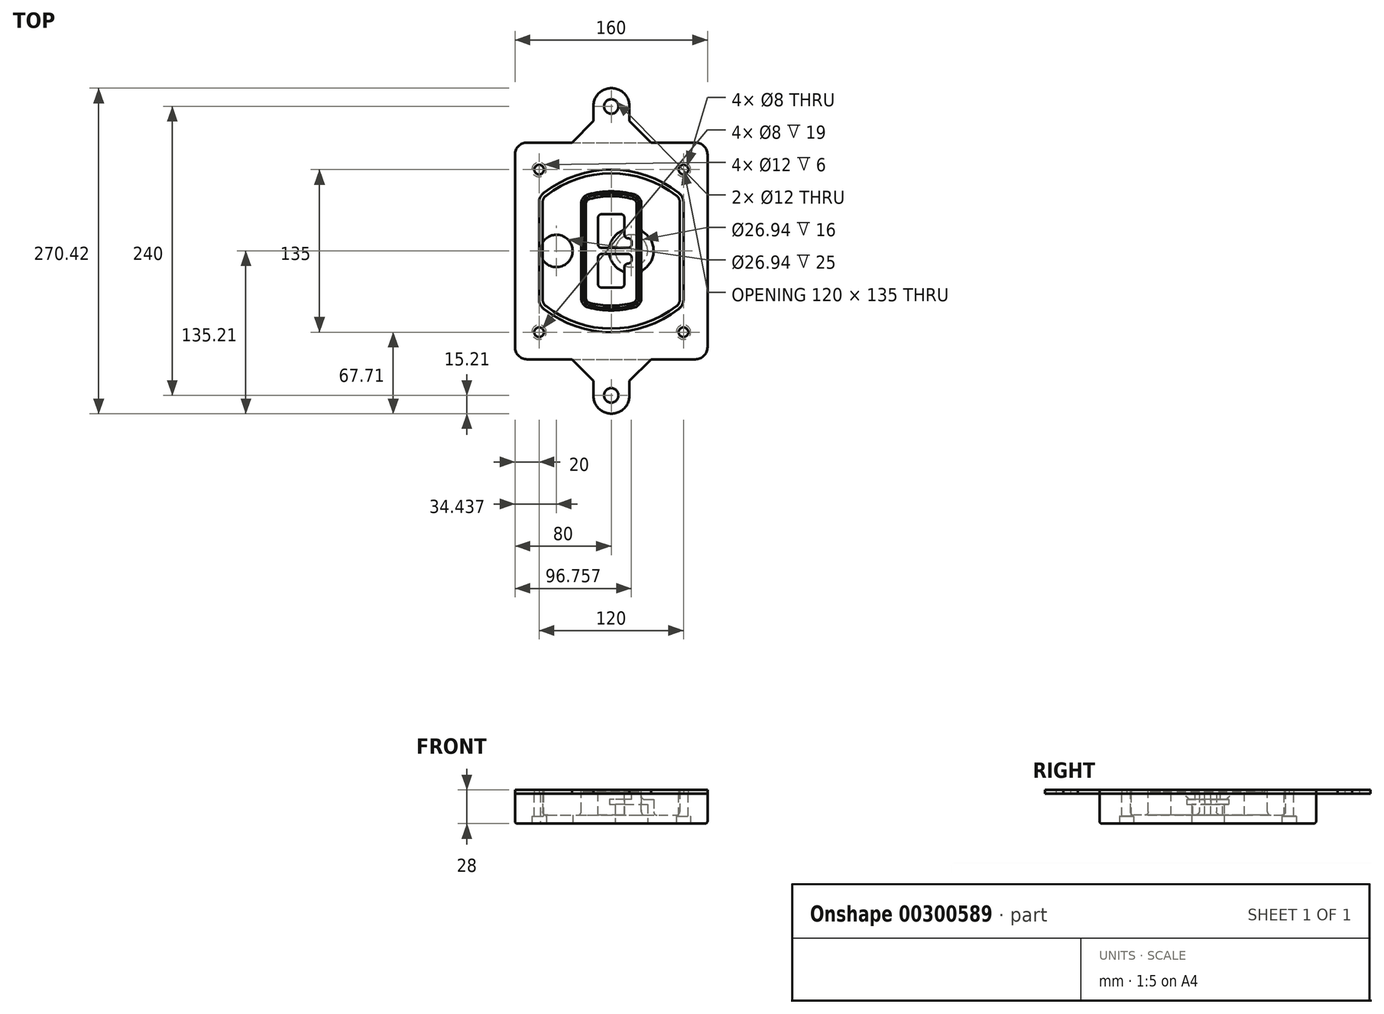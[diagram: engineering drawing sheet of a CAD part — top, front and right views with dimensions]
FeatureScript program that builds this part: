
annotation { "Feature Type Name" : "Feature", "Feature Type Description" : "" }
export const myFeature = defineFeature(function(context is Context, id is Id, definition is map)
    precondition{}
    {
        {
            var Q0;
            Q0=qCreatedBy(makeId("Top.planeOp"),FACE);
            var sketch = newSketch(context, id + "F0", { "sketchPlane" : qUnion([Q0])});
            skPoint(sketch, "E0.rect.middle", {"position": v(0, 0) * mm});
            skLineSegment(sketch, "E1.bottom", {"start": v(-70, -90) * mm, "end": v(70, -90) * mm});
            skLineSegment(sketch, "E1.top", {"start": v(-70, 90) * mm, "end": v(70, 90) * mm});
            skLineSegment(sketch, "E1.left", {"start": v(-80, -80) * mm, "end": v(-80, 80) * mm});
            skLineSegment(sketch, "E1.right", {"start": v(80, -80) * mm, "end": v(80, 80) * mm});
            skLineSegment(sketch, "E2", {"start": v(-80, 90) * mm, "end": v(80, -90) * mm, "construction": true});
            skLineSegment(sketch, "E3", {"start": v(80, 90) * mm, "end": v(-80, -90) * mm, "construction": true});
            skCircle(sketch, "E4", {"center": v(-60, 67.5) * mm, "radius": 4 * mm});
            skCircle(sketch, "E5", {"center": v(60, 67.5) * mm, "radius": 4 * mm});
            skCircle(sketch, "E6", {"center": v(60, -67.5) * mm, "radius": 4 * mm});
            skCircle(sketch, "E7", {"center": v(-60, -67.5) * mm, "radius": 4 * mm});
            skLineSegment(sketch, "E8", {"start": v(-60, 67.5) * mm, "end": v(60, 67.5) * mm, "construction": true});
            skLineSegment(sketch, "E9", {"start": v(60, 67.5) * mm, "end": v(60, -67.5) * mm, "construction": true});
            skLineSegment(sketch, "E10", {"start": v(60, -67.5) * mm, "end": v(-60, -67.5) * mm, "construction": true});
            skLineSegment(sketch, "E11", {"start": v(-60, -67.5) * mm, "end": v(-60, 67.5) * mm, "construction": true});
            skLineSegment(sketch, "E12", {"start": v(-60, 40.3) * mm, "end": v(-60, -40.3) * mm});
            skLineSegment(sketch, "E13", {"start": v(60, 40.3) * mm, "end": v(60, -40.3) * mm});
            skArc(sketch, "E14", {"start": v(56.15, 48.18) * mm, "mid": v(0, 67.5) * mm, "end": v(-56.15, 48.18) * mm});
            skArc(sketch, "E15", {"start": v(-56.15, -48.18) * mm, "mid": v(0, -67.5) * mm, "end": v(56.15, -48.18) * mm});
            skLineSegment(sketch, "E16", {"start": v(-60, 0) * mm, "end": v(60, 0) * mm, "construction": true});
            skPoint(sketch, "E17.visualSharp", {"position": v(-60, -45) * mm});
            skArc(sketch, "E17.filletArc", {"start": v(-60, -40.3) * mm, "mid": v(-58.99, -44.68) * mm, "end": v(-56.15, -48.18) * mm});
            skPoint(sketch, "E18.visualSharp", {"position": v(-60, 45) * mm});
            skArc(sketch, "E18.filletArc", {"start": v(-56.15, 48.18) * mm, "mid": v(-58.99, 44.68) * mm, "end": v(-60, 40.3) * mm});
            skPoint(sketch, "E19.visualSharp", {"position": v(60, 45) * mm});
            skArc(sketch, "E19.filletArc", {"start": v(60, 40.3) * mm, "mid": v(58.99, 44.68) * mm, "end": v(56.15, 48.18) * mm});
            skPoint(sketch, "E20.visualSharp", {"position": v(60, -45) * mm});
            skArc(sketch, "E20.filletArc", {"start": v(56.15, -48.18) * mm, "mid": v(58.99, -44.68) * mm, "end": v(60, -40.3) * mm});
            skPoint(sketch, "E21.visualSharp", {"position": v(-80, 90) * mm});
            skArc(sketch, "E21.filletArc", {"start": v(-70, 90) * mm, "mid": v(-77.07, 87.07) * mm, "end": v(-80, 80) * mm});
            skPoint(sketch, "E22.visualSharp", {"position": v(80, 90) * mm});
            skArc(sketch, "E22.filletArc", {"start": v(80, 80) * mm, "mid": v(77.07, 87.07) * mm, "end": v(70, 90) * mm});
            skPoint(sketch, "E23.visualSharp", {"position": v(80, -90) * mm});
            skArc(sketch, "E23.filletArc", {"start": v(70, -90) * mm, "mid": v(77.07, -87.07) * mm, "end": v(80, -80) * mm});
            skPoint(sketch, "E24.visualSharp", {"position": v(-80, -90) * mm});
            skArc(sketch, "E24.filletArc", {"start": v(-80, -80) * mm, "mid": v(-77.07, -87.07) * mm, "end": v(-70, -90) * mm});
            skArc(sketch, "E25.0", {"start": v(57, 40.3) * mm, "mid": v(56.3, 43.36) * mm, "end": v(54.3, 45.81) * mm});
            skLineSegment(sketch, "E25.1", {"start": v(57, 40.3) * mm, "end": v(57, -40.3) * mm});
            skArc(sketch, "E25.2", {"start": v(54.3, -45.81) * mm, "mid": v(56.3, -43.36) * mm, "end": v(57, -40.3) * mm});
            skArc(sketch, "E25.3", {"start": v(-54.3, -45.81) * mm, "mid": v(0, -64.5) * mm, "end": v(54.3, -45.81) * mm});
            skArc(sketch, "E25.4", {"start": v(-57, -40.3) * mm, "mid": v(-56.3, -43.36) * mm, "end": v(-54.3, -45.81) * mm});
            skArc(sketch, "E25.5", {"start": v(54.3, 45.81) * mm, "mid": v(0, 64.5) * mm, "end": v(-54.3, 45.81) * mm});
            skLineSegment(sketch, "E25.6", {"start": v(-57, 40.3) * mm, "end": v(-57, -40.3) * mm});
            skArc(sketch, "E25.7", {"start": v(-54.3, 45.81) * mm, "mid": v(-56.3, 43.36) * mm, "end": v(-57, 40.3) * mm});
            skArc(sketch, "E26.0", {"start": v(-58.62, 51.33) * mm, "mid": v(-62.58, 46.43) * mm, "end": v(-64, 40.3) * mm});
            skArc(sketch, "E26.1", {"start": v(58.62, 51.33) * mm, "mid": v(0, 71.5) * mm, "end": v(-58.62, 51.33) * mm});
            skArc(sketch, "E26.2", {"start": v(64, 40.3) * mm, "mid": v(62.58, 46.43) * mm, "end": v(58.62, 51.33) * mm});
            skLineSegment(sketch, "E26.3", {"start": v(64, 40.3) * mm, "end": v(64, -40.3) * mm});
            skArc(sketch, "E26.4", {"start": v(58.62, -51.33) * mm, "mid": v(62.58, -46.43) * mm, "end": v(64, -40.3) * mm});
            skLineSegment(sketch, "E26.5", {"start": v(-64, 40.3) * mm, "end": v(-64, -40.3) * mm});
            skArc(sketch, "E26.6", {"start": v(-58.62, -51.33) * mm, "mid": v(0, -71.5) * mm, "end": v(58.62, -51.33) * mm});
            skArc(sketch, "E26.7", {"start": v(-64, -40.3) * mm, "mid": v(-62.58, -46.43) * mm, "end": v(-58.62, -51.33) * mm});
            skSolve(sketch);
        }
        {
            var Q0;
            Q0=makeQuery(id+"F0.imprint","IMPRINT",FACE,{"disambiguationData":[TD([[makeQuery(id+"F0.imprint","IMPRINT",EDGE,{"derivedFrom":sQuery(id+"F0.wireOp",EDGE,"E1.bottom")}),1.0]])]});
            var Q1;
            Q1=makeQuery(id+"F0.imprint","IMPRINT",FACE,{"disambiguationData":[TD([[makeQuery(id+"F0.imprint","IMPRINT",EDGE,{"derivedFrom":sQuery(id+"F0.wireOp",EDGE,"E12")}),1.0]])]});
            var Q2;
            Q2=makeQuery(id+"F0.imprint","IMPRINT",FACE,{"disambiguationData":[TD([[makeQuery(id+"F0.imprint","IMPRINT",EDGE,{"derivedFrom":sQuery(id+"F0.wireOp",EDGE,"E25.0")}),1.0]])]});
            var Q3;
            Q3=makeQuery(id+"F0.imprint","IMPRINT",FACE,{"disambiguationData":[TD([[makeQuery(id+"F0.imprint","IMPRINT",EDGE,{"derivedFrom":sQuery(id+"F0.wireOp",EDGE,"E12")}),-1.0]])]});
            extrude(context, id + "F1", {"entities" : qUnion([Q0, Q1, Q2, Q3]), "oppositeDirection" : true, "depth" : 25 * mm});
        }
        {
            var Q0;
            Q0=makeQuery(id+"F0.imprint","IMPRINT",FACE,{"disambiguationData":[TD([[makeQuery(id+"F0.imprint","IMPRINT",EDGE,{"derivedFrom":sQuery(id+"F0.wireOp",EDGE,"E12")}),1.0]])]});
            extrude(context, id + "F2", {"entities" : qUnion([Q0]), "operationType" : NewBodyOperationType.ADD, "depth" : 3 * mm});
        }
        {
            var Q0;
            Q0=makeQuery(id+"F0.imprint","IMPRINT",FACE,{"disambiguationData":[TD([[makeQuery(id+"F0.imprint","IMPRINT",EDGE,{"derivedFrom":sQuery(id+"F0.wireOp",EDGE,"E25.0")}),1.0]])]});
            extrude(context, id + "F3", {"entities" : qUnion([Q0]), "operationType" : NewBodyOperationType.REMOVE, "oppositeDirection" : true, "depth" : 18 * mm});
        }
        {
            var Q0;
            Q0=makeQuery(id+"F2.opExtrude","CAP_FACE",FACE,{"disambiguationData":[OSD([sQuery(id+"F0.wireOp",EDGE,"E12"),sQuery(id+"F0.wireOp",EDGE,"E13"),sQuery(id+"F0.wireOp",EDGE,"E14"),sQuery(id+"F0.wireOp",EDGE,"E15"),sQuery(id+"F0.wireOp",EDGE,"E17.filletArc"),sQuery(id+"F0.wireOp",EDGE,"E18.filletArc"),sQuery(id+"F0.wireOp",EDGE,"E19.filletArc"),sQuery(id+"F0.wireOp",EDGE,"E20.filletArc"),sQuery(id+"F0.wireOp",EDGE,"E25.0"),sQuery(id+"F0.wireOp",EDGE,"E25.1"),sQuery(id+"F0.wireOp",EDGE,"E25.2"),sQuery(id+"F0.wireOp",EDGE,"E25.3"),sQuery(id+"F0.wireOp",EDGE,"E25.4"),sQuery(id+"F0.wireOp",EDGE,"E25.5"),sQuery(id+"F0.wireOp",EDGE,"E25.6"),sQuery(id+"F0.wireOp",EDGE,"E25.7")])],"isStart":false});
            var sketch = newSketch(context, id + "F4", { "sketchPlane" : qUnion([Q0])});
            skArc(sketch, "E27.0", {"start": v(-19.08, -46.97) * mm, "mid": v(0, -49.5) * mm, "end": v(19.08, -46.97) * mm});
            skArc(sketch, "E28.0", {"start": v(19.08, 46.97) * mm, "mid": v(0, 49.5) * mm, "end": v(-19.08, 46.97) * mm});
            skLineSegment(sketch, "E29", {"start": v(-25, 39.25) * mm, "end": v(-25, -39.25) * mm});
            skLineSegment(sketch, "E30", {"start": v(25, 39.25) * mm, "end": v(25, -39.25) * mm});
            skLineSegment(sketch, "E31", {"start": v(-25, 45.1) * mm, "end": v(25, 45.1) * mm, "construction": true});
            skLineSegment(sketch, "E32", {"start": v(-25, -45.1) * mm, "end": v(25, -45.1) * mm, "construction": true});
            skPoint(sketch, "E33.visualSharp", {"position": v(-25, 45.1) * mm});
            skArc(sketch, "E33.filletArc", {"start": v(-19.08, 46.97) * mm, "mid": v(-23.35, 44.11) * mm, "end": v(-25, 39.25) * mm});
            skPoint(sketch, "E34.visualSharp", {"position": v(25, 45.1) * mm});
            skArc(sketch, "E34.filletArc", {"start": v(25, 39.25) * mm, "mid": v(23.35, 44.11) * mm, "end": v(19.08, 46.97) * mm});
            skPoint(sketch, "E35.visualSharp", {"position": v(25, -45.1) * mm});
            skArc(sketch, "E35.filletArc", {"start": v(19.08, -46.97) * mm, "mid": v(23.35, -44.11) * mm, "end": v(25, -39.25) * mm});
            skPoint(sketch, "E36.visualSharp", {"position": v(-25, -45.1) * mm});
            skArc(sketch, "E36.filletArc", {"start": v(-25, -39.25) * mm, "mid": v(-23.35, -44.11) * mm, "end": v(-19.08, -46.97) * mm});
            skArc(sketch, "E37.0", {"start": v(54.3, 45.81) * mm, "mid": v(0, 64.5) * mm, "end": v(-54.3, 45.81) * mm});
            skArc(sketch, "E37.1", {"start": v(-54.3, 45.81) * mm, "mid": v(-56.3, 43.36) * mm, "end": v(-57, 40.3) * mm});
            skLineSegment(sketch, "E37.2", {"start": v(-57, 40.3) * mm, "end": v(-57, -40.3) * mm});
            skArc(sketch, "E37.3", {"start": v(-57, -40.3) * mm, "mid": v(-56.3, -43.36) * mm, "end": v(-54.3, -45.81) * mm});
            skArc(sketch, "E37.4", {"start": v(-54.3, -45.81) * mm, "mid": v(0, -64.5) * mm, "end": v(54.3, -45.81) * mm});
            skArc(sketch, "E37.5", {"start": v(54.3, -45.81) * mm, "mid": v(56.3, -43.36) * mm, "end": v(57, -40.3) * mm});
            skLineSegment(sketch, "E37.6", {"start": v(57, 40.3) * mm, "end": v(57, -40.3) * mm});
            skArc(sketch, "E37.7", {"start": v(57, 40.3) * mm, "mid": v(56.3, 43.36) * mm, "end": v(54.3, 45.81) * mm});
            skLineSegment(sketch, "E38.0", {"start": v(23, 39.25) * mm, "end": v(23, -39.25) * mm});
            skArc(sketch, "E38.1", {"start": v(18.56, -45.04) * mm, "mid": v(21.76, -42.9) * mm, "end": v(23, -39.25) * mm});
            skArc(sketch, "E38.2", {"start": v(-18.56, -45.04) * mm, "mid": v(0, -47.5) * mm, "end": v(18.56, -45.04) * mm});
            skArc(sketch, "E38.3", {"start": v(-23, -39.25) * mm, "mid": v(-21.76, -42.9) * mm, "end": v(-18.56, -45.04) * mm});
            skLineSegment(sketch, "E38.4", {"start": v(-23, 39.25) * mm, "end": v(-23, -39.25) * mm});
            skArc(sketch, "E38.5", {"start": v(23, 39.25) * mm, "mid": v(21.76, 42.9) * mm, "end": v(18.56, 45.04) * mm});
            skArc(sketch, "E38.6", {"start": v(-18.56, 45.04) * mm, "mid": v(-21.76, 42.9) * mm, "end": v(-23, 39.25) * mm});
            skArc(sketch, "E38.7", {"start": v(18.56, 45.04) * mm, "mid": v(0, 47.5) * mm, "end": v(-18.56, 45.04) * mm});
            skArc(sketch, "E39.0", {"start": v(21, 39.25) * mm, "mid": v(20.18, 41.68) * mm, "end": v(18.04, 43.1) * mm});
            skLineSegment(sketch, "E39.1", {"start": v(21, 39.25) * mm, "end": v(21, -39.25) * mm});
            skArc(sketch, "E39.2", {"start": v(18.04, -43.1) * mm, "mid": v(20.18, -41.68) * mm, "end": v(21, -39.25) * mm});
            skArc(sketch, "E39.3", {"start": v(-18.04, -43.1) * mm, "mid": v(0, -45.5) * mm, "end": v(18.04, -43.1) * mm});
            skArc(sketch, "E39.4", {"start": v(-21, -39.25) * mm, "mid": v(-20.18, -41.68) * mm, "end": v(-18.04, -43.1) * mm});
            skArc(sketch, "E39.5", {"start": v(18.04, 43.1) * mm, "mid": v(0, 45.5) * mm, "end": v(-18.04, 43.1) * mm});
            skLineSegment(sketch, "E39.6", {"start": v(-21, 39.25) * mm, "end": v(-21, -39.25) * mm});
            skArc(sketch, "E39.7", {"start": v(-18.04, 43.1) * mm, "mid": v(-20.18, 41.68) * mm, "end": v(-21, 39.25) * mm});
            skLineSegment(sketch, "E40", {"start": v(-25, 0) * mm, "end": v(25, 0) * mm, "construction": true});
            skLineSegment(sketch, "E41", {"start": v(-11, 5.5) * mm, "end": v(-11, 27.5) * mm});
            skLineSegment(sketch, "E42", {"start": v(-8, 30.5) * mm, "end": v(8, 30.5) * mm});
            skLineSegment(sketch, "E43", {"start": v(11, 27.5) * mm, "end": v(11, 13.5) * mm});
            skLineSegment(sketch, "E44", {"start": v(14, 10.5) * mm, "end": v(14, 10.5) * mm});
            skLineSegment(sketch, "E45", {"start": v(17, 7.5) * mm, "end": v(17, 5.5) * mm});
            skLineSegment(sketch, "E46", {"start": v(14, 2.5) * mm, "end": v(-8, 2.5) * mm});
            skPoint(sketch, "E47.visualSharp", {"position": v(-11, 30.5) * mm});
            skArc(sketch, "E47.filletArc", {"start": v(-8, 30.5) * mm, "mid": v(-10.12, 29.62) * mm, "end": v(-11, 27.5) * mm});
            skPoint(sketch, "E48.visualSharp", {"position": v(11, 30.5) * mm});
            skArc(sketch, "E48.filletArc", {"start": v(11, 27.5) * mm, "mid": v(10.12, 29.62) * mm, "end": v(8, 30.5) * mm});
            skPoint(sketch, "E49.visualSharp", {"position": v(11, 10.5) * mm});
            skArc(sketch, "E49.filletArc", {"start": v(11, 13.5) * mm, "mid": v(11.88, 11.38) * mm, "end": v(14, 10.5) * mm});
            skPoint(sketch, "E50.visualSharp", {"position": v(17, 10.5) * mm});
            skArc(sketch, "E50.filletArc", {"start": v(17, 7.5) * mm, "mid": v(16.12, 9.62) * mm, "end": v(14, 10.5) * mm});
            skPoint(sketch, "E51.visualSharp", {"position": v(17, 2.5) * mm});
            skArc(sketch, "E51.filletArc", {"start": v(14, 2.5) * mm, "mid": v(16.12, 3.38) * mm, "end": v(17, 5.5) * mm});
            skPoint(sketch, "E52.visualSharp", {"position": v(-11, 2.5) * mm});
            skArc(sketch, "E52.filletArc", {"start": v(-11, 5.5) * mm, "mid": v(-10.12, 3.38) * mm, "end": v(-8, 2.5) * mm});
            skLineSegment(sketch, "E53.0.MirrorCS", {"start": v(14, -2.5) * mm, "end": v(-8, -2.5) * mm});
            skArc(sketch, "E54.0.MirrorCS", {"start": v(-11, -5.5) * mm, "mid": v(-10.12, -3.38) * mm, "end": v(-8, -2.5) * mm});
            skLineSegment(sketch, "E55.0.MirrorCS", {"start": v(-11, -5.5) * mm, "end": v(-11, -27.5) * mm});
            skArc(sketch, "E56.0.MirrorCS", {"start": v(-8, -30.5) * mm, "mid": v(-10.12, -29.62) * mm, "end": v(-11, -27.5) * mm});
            skLineSegment(sketch, "E57.0.MirrorCS", {"start": v(-8, -30.5) * mm, "end": v(8, -30.5) * mm});
            skArc(sketch, "E58.0.MirrorCS", {"start": v(11, -27.5) * mm, "mid": v(10.12, -29.62) * mm, "end": v(8, -30.5) * mm});
            skLineSegment(sketch, "E59.0.MirrorCS", {"start": v(11, -27.5) * mm, "end": v(11, -13.5) * mm});
            skArc(sketch, "E60.0.MirrorCS", {"start": v(11, -13.5) * mm, "mid": v(11.88, -11.38) * mm, "end": v(14, -10.5) * mm});
            skArc(sketch, "E61.0.MirrorCS", {"start": v(17, -7.5) * mm, "mid": v(16.12, -9.62) * mm, "end": v(14, -10.5) * mm});
            skLineSegment(sketch, "E62.0.MirrorCS", {"start": v(17, -7.5) * mm, "end": v(17, -5.5) * mm});
            skArc(sketch, "E63.0.MirrorCS", {"start": v(14, -2.5) * mm, "mid": v(16.12, -3.38) * mm, "end": v(17, -5.5) * mm});
            skSolve(sketch);
        }
        {
            var Q0;
            Q0=makeQuery(id+"F4.imprint","IMPRINT",FACE,{"disambiguationData":[TD([[makeQuery(id+"F4.imprint","IMPRINT",EDGE,{"derivedFrom":sQuery(id+"F4.wireOp",EDGE,"E27.0")}),1.0]])]});
            var Q1;
            Q1=makeQuery(id+"F4.imprint","IMPRINT",FACE,{"disambiguationData":[TD([[makeQuery(id+"F4.imprint","IMPRINT",EDGE,{"derivedFrom":sQuery(id+"F4.wireOp",EDGE,"E38.0")}),-1.0]])]});
            var Q2;
            Q2=makeQuery(id+"F4.imprint","IMPRINT",FACE,{"disambiguationData":[TD([[makeQuery(id+"F4.imprint","IMPRINT",EDGE,{"derivedFrom":sQuery(id+"F4.wireOp",EDGE,"E39.0")}),1.0]])]});
            extrude(context, id + "F5", {"entities" : qUnion([Q0, Q1, Q2]), "operationType" : NewBodyOperationType.ADD, "endBound" : BoundingType.UP_TO_NEXT, "oppositeDirection" : true, "depth" : 25 * mm});
        }
        {
            var Q0;
            Q0=makeQuery(id+"F4.imprint","IMPRINT",FACE,{"disambiguationData":[TD([[makeQuery(id+"F4.imprint","IMPRINT",EDGE,{"derivedFrom":sQuery(id+"F4.wireOp",EDGE,"E38.0")}),-1.0]])]});
            extrude(context, id + "F6", {"entities" : qUnion([Q0]), "operationType" : NewBodyOperationType.REMOVE, "oppositeDirection" : true, "depth" : 2 * mm});
        }
        {
            var Q0;
            Q0=makeQuery(id+"F1.opExtrude","CAP_FACE",FACE,{"disambiguationData":[OSD([sQuery(id+"F0.wireOp",EDGE,"E1.bottom"),sQuery(id+"F0.wireOp",EDGE,"E1.top"),sQuery(id+"F0.wireOp",EDGE,"E1.left"),sQuery(id+"F0.wireOp",EDGE,"E1.right"),sQuery(id+"F0.wireOp",EDGE,"E4"),sQuery(id+"F0.wireOp",EDGE,"E5"),sQuery(id+"F0.wireOp",EDGE,"E6"),sQuery(id+"F0.wireOp",EDGE,"E7"),sQuery(id+"F0.wireOp",EDGE,"E21.filletArc"),sQuery(id+"F0.wireOp",EDGE,"E22.filletArc"),sQuery(id+"F0.wireOp",EDGE,"E23.filletArc"),sQuery(id+"F0.wireOp",EDGE,"E24.filletArc")])],"isStart":false});
            var sketch = newSketch(context, id + "F7", { "sketchPlane" : qUnion([Q0])});
            skCircle(sketch, "E64", {"center": v(16.76, 0) * mm, "radius": 13.47 * mm});
            skCircle(sketch, "E65", {"center": v(-45.56, 0) * mm, "radius": 13.47 * mm});
            skLineSegment(sketch, "E66", {"start": v(80, 0) * mm, "end": v(-80, 0) * mm});
            skCircle(sketch, "E67", {"center": v(16.76, 0) * mm, "radius": 18.47 * mm});
            skCircle(sketch, "E68", {"center": v(60, -67.5) * mm, "radius": 6 * mm});
            skCircle(sketch, "E69", {"center": v(-60, -67.5) * mm, "radius": 6 * mm});
            skCircle(sketch, "E70", {"center": v(-60, 67.5) * mm, "radius": 6 * mm});
            skCircle(sketch, "E71", {"center": v(60, 67.5) * mm, "radius": 6 * mm});
            skSolve(sketch);
        }
        {
            var Q0;
            {var subQ1=sQuery(id+"F7.wireOp",EDGE,"E66");var subQ4=sQuery(id+"F7.wireOp",EDGE,"E64");var subQ6=makeQuery(id+"F7.imprint","INTERSECT",VERTEX,{"disambiguationData":[OD(0.0)],"derivedFrom":[subQ4,subQ1]});Q0=makeQuery(id+"F7.imprint","IMPRINT",FACE,{"disambiguationData":[TD([[makeQuery(id+"F7.imprint","IMPRINT",EDGE,{"disambiguationData":[TD([[subQ6,-1.0]])],"derivedFrom":subQ4}),-1.0]])]});}
            var Q1;
            {var subQ0=sQuery(id+"F7.wireOp",EDGE,"E66");var subQ1=sQuery(id+"F7.wireOp",EDGE,"E64");var subQ3=makeQuery(id+"F7.imprint","INTERSECT",VERTEX,{"disambiguationData":[OD(0.0)],"derivedFrom":[subQ1,subQ0]});Q1=makeQuery(id+"F7.imprint","IMPRINT",FACE,{"disambiguationData":[TD([[makeQuery(id+"F7.imprint","IMPRINT",EDGE,{"disambiguationData":[TD([[subQ3,-1.0]])],"derivedFrom":subQ1}),1.0]])]});}
            var Q2;
            {var subQ0=sQuery(id+"F7.wireOp",EDGE,"E66");var subQ1=sQuery(id+"F7.wireOp",EDGE,"E64");var subQ3=makeQuery(id+"F7.imprint","INTERSECT",VERTEX,{"disambiguationData":[OD(0.0)],"derivedFrom":[subQ1,subQ0]});Q2=makeQuery(id+"F7.imprint","IMPRINT",FACE,{"disambiguationData":[TD([[makeQuery(id+"F7.imprint","IMPRINT",EDGE,{"disambiguationData":[TD([[subQ3,1.0]])],"derivedFrom":subQ1}),1.0]])]});}
            var Q3;
            {var subQ1=sQuery(id+"F7.wireOp",EDGE,"E66");var subQ4=sQuery(id+"F7.wireOp",EDGE,"E64");var subQ6=makeQuery(id+"F7.imprint","INTERSECT",VERTEX,{"disambiguationData":[OD(0.0)],"derivedFrom":[subQ4,subQ1]});Q3=makeQuery(id+"F7.imprint","IMPRINT",FACE,{"disambiguationData":[TD([[makeQuery(id+"F7.imprint","IMPRINT",EDGE,{"disambiguationData":[TD([[subQ6,1.0]])],"derivedFrom":subQ4}),-1.0]])]});}
            extrude(context, id + "F8", {"entities" : qUnion([Q0, Q1, Q2, Q3]), "operationType" : NewBodyOperationType.ADD, "oppositeDirection" : true, "depth" : 20 * mm});
        }
        {
            var Q0;
            {var subQ0=sQuery(id+"F7.wireOp",EDGE,"E66");var subQ1=sQuery(id+"F7.wireOp",EDGE,"E64");var subQ3=makeQuery(id+"F7.imprint","INTERSECT",VERTEX,{"disambiguationData":[OD(0.0)],"derivedFrom":[subQ1,subQ0]});Q0=makeQuery(id+"F7.imprint","IMPRINT",FACE,{"disambiguationData":[TD([[makeQuery(id+"F7.imprint","IMPRINT",EDGE,{"disambiguationData":[TD([[subQ3,-1.0]])],"derivedFrom":subQ1}),1.0]])]});}
            var Q1;
            {var subQ0=sQuery(id+"F7.wireOp",EDGE,"E66");var subQ1=sQuery(id+"F7.wireOp",EDGE,"E64");var subQ3=makeQuery(id+"F7.imprint","INTERSECT",VERTEX,{"disambiguationData":[OD(0.0)],"derivedFrom":[subQ1,subQ0]});Q1=makeQuery(id+"F7.imprint","IMPRINT",FACE,{"disambiguationData":[TD([[makeQuery(id+"F7.imprint","IMPRINT",EDGE,{"disambiguationData":[TD([[subQ3,1.0]])],"derivedFrom":subQ1}),1.0]])]});}
            extrude(context, id + "F9", {"entities" : qUnion([Q0, Q1]), "operationType" : NewBodyOperationType.REMOVE, "oppositeDirection" : true, "depth" : 16 * mm});
        }
        {
            var Q0;
            {var subQ0=sQuery(id+"F7.wireOp",EDGE,"E66");var subQ1=sQuery(id+"F7.wireOp",EDGE,"E65");var subQ3=makeQuery(id+"F7.imprint","INTERSECT",VERTEX,{"disambiguationData":[OD(0.0)],"derivedFrom":[subQ1,subQ0]});Q0=makeQuery(id+"F7.imprint","IMPRINT",FACE,{"disambiguationData":[TD([[makeQuery(id+"F7.imprint","IMPRINT",EDGE,{"disambiguationData":[TD([[subQ3,-1.0]])],"derivedFrom":subQ1}),1.0]])]});}
            var Q1;
            {var subQ0=sQuery(id+"F7.wireOp",EDGE,"E66");var subQ1=sQuery(id+"F7.wireOp",EDGE,"E65");var subQ3=makeQuery(id+"F7.imprint","INTERSECT",VERTEX,{"disambiguationData":[OD(0.0)],"derivedFrom":[subQ1,subQ0]});Q1=makeQuery(id+"F7.imprint","IMPRINT",FACE,{"disambiguationData":[TD([[makeQuery(id+"F7.imprint","IMPRINT",EDGE,{"disambiguationData":[TD([[subQ3,1.0]])],"derivedFrom":subQ1}),1.0]])]});}
            extrude(context, id + "F10", {"entities" : qUnion([Q0, Q1]), "operationType" : NewBodyOperationType.REMOVE, "oppositeDirection" : true, "depth" : 25 * mm});
        }
        {
            var Q0;
            Q0=makeQuery(id+"F7.imprint","IMPRINT",FACE,{"disambiguationData":[TD([[makeQuery(id+"F7.imprint","IMPRINT",EDGE,{"derivedFrom":sQuery(id+"F7.wireOp",EDGE,"E68")}),1.0]])]});
            var Q1;
            Q1=makeQuery(id+"F7.imprint","IMPRINT",FACE,{"disambiguationData":[TD([[makeQuery(id+"F7.imprint","IMPRINT",EDGE,{"derivedFrom":makeQuery(id+"F1.opExtrude","CAP_EDGE",EDGE,{"disambiguationData":[OSD([sQuery(id+"F0.wireOp",EDGE,"E5")])],"isStart":false})}),-1.0]])]});
            var Q2;
            Q2=makeQuery(id+"F7.imprint","IMPRINT",FACE,{"disambiguationData":[TD([[makeQuery(id+"F7.imprint","IMPRINT",EDGE,{"derivedFrom":sQuery(id+"F7.wireOp",EDGE,"E69")}),1.0]])]});
            var Q3;
            Q3=makeQuery(id+"F7.imprint","IMPRINT",FACE,{"disambiguationData":[TD([[makeQuery(id+"F7.imprint","IMPRINT",EDGE,{"derivedFrom":makeQuery(id+"F1.opExtrude","CAP_EDGE",EDGE,{"disambiguationData":[OSD([sQuery(id+"F0.wireOp",EDGE,"E4")])],"isStart":false})}),-1.0]])]});
            var Q4;
            Q4=makeQuery(id+"F7.imprint","IMPRINT",FACE,{"disambiguationData":[TD([[makeQuery(id+"F7.imprint","IMPRINT",EDGE,{"derivedFrom":sQuery(id+"F7.wireOp",EDGE,"E70")}),1.0]])]});
            var Q5;
            Q5=makeQuery(id+"F7.imprint","IMPRINT",FACE,{"disambiguationData":[TD([[makeQuery(id+"F7.imprint","IMPRINT",EDGE,{"derivedFrom":makeQuery(id+"F1.opExtrude","CAP_EDGE",EDGE,{"disambiguationData":[OSD([sQuery(id+"F0.wireOp",EDGE,"E7")])],"isStart":false})}),-1.0]])]});
            var Q6;
            Q6=makeQuery(id+"F7.imprint","IMPRINT",FACE,{"disambiguationData":[TD([[makeQuery(id+"F7.imprint","IMPRINT",EDGE,{"derivedFrom":sQuery(id+"F7.wireOp",EDGE,"E71")}),1.0]])]});
            var Q7;
            Q7=makeQuery(id+"F7.imprint","IMPRINT",FACE,{"disambiguationData":[TD([[makeQuery(id+"F7.imprint","IMPRINT",EDGE,{"derivedFrom":makeQuery(id+"F1.opExtrude","CAP_EDGE",EDGE,{"disambiguationData":[OSD([sQuery(id+"F0.wireOp",EDGE,"E6")])],"isStart":false})}),-1.0]])]});
            extrude(context, id + "F11", {"entities" : qUnion([Q0, Q1, Q2, Q3, Q4, Q5, Q6, Q7]), "operationType" : NewBodyOperationType.REMOVE, "oppositeDirection" : true, "depth" : 6 * mm});
        }
        {
            var Q0;
            Q0=makeQuery(id+"F9.boolean.opBoolean","COPY",FACE,{"derivedFrom":makeQuery(id+"F9.opExtrude","CAP_FACE",FACE,{"disambiguationData":[OSD([sQuery(id+"F7.wireOp",EDGE,"E64")])],"isStart":false})});
            var sketch = newSketch(context, id + "F12", { "sketchPlane" : qUnion([Q0])});
            skArc(sketch, "E72.0", {"start": v(11, 17.55) * mm, "mid": v(2.57, 11.82) * mm, "end": v(-1.54, 2.5) * mm});
            skArc(sketch, "E72.1", {"start": v(-1.54, -2.5) * mm, "mid": v(2.57, -11.82) * mm, "end": v(11, -17.55) * mm});
            skLineSegment(sketch, "E73", {"start": v(-1.54, -2.5) * mm, "end": v(14, -2.5) * mm});
            skLineSegment(sketch, "E74.0", {"start": v(14, 2.5) * mm, "end": v(-1.54, 2.5) * mm});
            skArc(sketch, "E74.1", {"start": v(14, 2.5) * mm, "mid": v(16.12, 3.38) * mm, "end": v(17, 5.5) * mm});
            skLineSegment(sketch, "E74.2", {"start": v(17, 7.5) * mm, "end": v(17, 5.5) * mm});
            skArc(sketch, "E74.3", {"start": v(17, 7.5) * mm, "mid": v(16.12, 9.62) * mm, "end": v(14, 10.5) * mm});
            skArc(sketch, "E74.4", {"start": v(11, 13.5) * mm, "mid": v(11.88, 11.38) * mm, "end": v(14, 10.5) * mm});
            skLineSegment(sketch, "E74.5", {"start": v(11, 17.55) * mm, "end": v(11, 13.5) * mm});
            skLineSegment(sketch, "E74.7", {"start": v(14, -2.5) * mm, "end": v(-1.54, -2.5) * mm});
            skArc(sketch, "E74.8", {"start": v(14, -2.5) * mm, "mid": v(16.12, -3.38) * mm, "end": v(17, -5.5) * mm});
            skLineSegment(sketch, "E74.9", {"start": v(17, -7.5) * mm, "end": v(17, -5.5) * mm});
            skArc(sketch, "E74.10", {"start": v(17, -7.5) * mm, "mid": v(16.12, -9.62) * mm, "end": v(14, -10.5) * mm});
            skArc(sketch, "E74.11", {"start": v(11, -13.5) * mm, "mid": v(11.88, -11.38) * mm, "end": v(14, -10.5) * mm});
            skLineSegment(sketch, "E74.12", {"start": v(11, -17.55) * mm, "end": v(11, -13.5) * mm});
            skPoint(sketch, "E75.orphan", {"position": v(11, -27.5) * mm});
            skPoint(sketch, "E76.orphan", {"position": v(-8, -2.5) * mm});
            skPoint(sketch, "E77.orphan", {"position": v(-8, 2.5) * mm});
            skPoint(sketch, "E78.orphan", {"position": v(11, 27.5) * mm});
            skSolve(sketch);
        }
        {
            var Q0;
            {var subQ7=sQuery(id+"F12.wireOp",EDGE,"E72.0");var subQ14=sQuery(id+"F12.wireOp",EDGE,"E72.1");var subQ16=sQuery(id+"F12.wireOp",EDGE,"E74.1");var subQ18=sQuery(id+"F12.wireOp",EDGE,"E74.8");Q0=qUnion([makeQuery(id+"F12.imprint","IMPRINT",FACE,{"disambiguationData":[TD([[makeQuery(id+"F12.imprint","IMPRINT",EDGE,{"derivedFrom":subQ7}),1.0]])]}),makeQuery(id+"F12.imprint","IMPRINT",FACE,{"disambiguationData":[TD([[makeQuery(id+"F12.imprint","IMPRINT",EDGE,{"derivedFrom":subQ14}),1.0]])]}),makeQuery(id+"F12.imprint","IMPRINT",FACE,{"disambiguationData":[TD([[makeQuery(id+"F12.imprint","IMPRINT",EDGE,{"derivedFrom":subQ16}),1.0]])]}),makeQuery(id+"F12.imprint","IMPRINT",FACE,{"disambiguationData":[TD([[makeQuery(id+"F12.imprint","IMPRINT",EDGE,{"derivedFrom":subQ18}),-1.0]])]})]);}
            var Q1;
            Q1=makeQuery(id+"F5.boolean.opBoolean","SPLIT",FACE,{"disambiguationData":[TD([makeQuery(id+"F5.opExtrude","SWEPT_FACE",FACE,{"disambiguationData":[OSD([sQuery(id+"F4.wireOp",EDGE,"E41")])]})])],"derivedFrom":makeQuery(id+"F3.boolean.opBoolean","COPY",FACE,{"derivedFrom":makeQuery(id+"F3.opExtrude","CAP_FACE",FACE,{"disambiguationData":[OSD([sQuery(id+"F0.wireOp",EDGE,"E25.0"),sQuery(id+"F0.wireOp",EDGE,"E25.1"),sQuery(id+"F0.wireOp",EDGE,"E25.2"),sQuery(id+"F0.wireOp",EDGE,"E25.3"),sQuery(id+"F0.wireOp",EDGE,"E25.4"),sQuery(id+"F0.wireOp",EDGE,"E25.5"),sQuery(id+"F0.wireOp",EDGE,"E25.6"),sQuery(id+"F0.wireOp",EDGE,"E25.7")])],"isStart":false})})});
            extrude(context, id + "F13", {"entities" : qUnion([Q0]), "operationType" : NewBodyOperationType.REMOVE, "endBound" : BoundingType.UP_TO_SURFACE, "endBoundEntityFace" : qUnion([Q1]), "depth" : 25 * mm});
        }
        {
            var Q0;
            Q0=makeQuery(id+"F3.boolean.opBoolean","COPY",EDGE,{"derivedFrom":makeQuery(id+"F3.opExtrude","CAP_EDGE",EDGE,{"disambiguationData":[OSD([sQuery(id+"F0.wireOp",EDGE,"E25.6")])],"isStart":false})});
            var Q1;
            Q1=makeQuery(id+"F8.boolean.opBoolean","INTERSECT",EDGE,{"derivedFrom":[makeQuery(id+"F5.opExtrude","SWEPT_FACE",FACE,{"disambiguationData":[OSD([sQuery(id+"F4.wireOp",EDGE,"E30")])]}),makeQuery(id+"F8.opExtrude","CAP_FACE",FACE,{"disambiguationData":[OSD([sQuery(id+"F7.wireOp",EDGE,"E67")])],"isStart":false})]});
            var Q2;
            Q2=makeQuery(id+"F8.boolean.opBoolean","INTERSECT",EDGE,{"disambiguationData":[OD(1.0)],"derivedFrom":[makeQuery(id+"F5.opExtrude","SWEPT_FACE",FACE,{"disambiguationData":[OSD([sQuery(id+"F4.wireOp",EDGE,"E30")])]}),makeQuery(id+"F8.opExtrude","SWEPT_FACE",FACE,{"disambiguationData":[OSD([sQuery(id+"F7.wireOp",EDGE,"E67")])]})]});
            var Q3;
            {var subQ0=sQuery(id+"F4.wireOp",EDGE,"E30");Q3=makeQuery(id+"F8.boolean.opBoolean","SPLIT",EDGE,{"disambiguationData":[TD([makeQuery(id+"F5.opExtrude","SWEPT_FACE",FACE,{"disambiguationData":[OSD([sQuery(id+"F4.wireOp",EDGE,"E35.filletArc")])]})])],"derivedFrom":makeQuery(id+"F5.opExtrude","CAP_EDGE",EDGE,{"disambiguationData":[OSD([subQ0])],"isStart":false})});}
            var Q4;
            {var subQ0=sQuery(id+"F0.wireOp",EDGE,"E25.7");var subQ1=sQuery(id+"F0.wireOp",EDGE,"E25.1");var subQ2=sQuery(id+"F0.wireOp",EDGE,"E25.6");var subQ3=sQuery(id+"F0.wireOp",EDGE,"E25.5");var subQ4=sQuery(id+"F0.wireOp",EDGE,"E25.4");var subQ5=sQuery(id+"F0.wireOp",EDGE,"E25.0");var subQ6=sQuery(id+"F0.wireOp",EDGE,"E25.2");var subQ7=sQuery(id+"F0.wireOp",EDGE,"E25.3");Q4=makeQuery(id+"F8.boolean.opBoolean","INTERSECT",EDGE,{"derivedFrom":[makeQuery(id+"F5.boolean.opBoolean","SPLIT",FACE,{"disambiguationData":[TD([makeQuery(id+"F2.opExtrude","SWEPT_FACE",FACE,{"disambiguationData":[OSD([subQ5])]})])],"derivedFrom":makeQuery(id+"F3.boolean.opBoolean","COPY",FACE,{"derivedFrom":makeQuery(id+"F3.opExtrude","CAP_FACE",FACE,{"disambiguationData":[OSD([subQ5,subQ1,subQ6,subQ7,subQ4,subQ3,subQ2,subQ0])],"isStart":false})})}),makeQuery(id+"F8.opExtrude","SWEPT_FACE",FACE,{"disambiguationData":[OSD([sQuery(id+"F7.wireOp",EDGE,"E67")])]})]});}
            var Q5;
            Q5=makeQuery(id+"F8.boolean.opBoolean","INTERSECT",EDGE,{"disambiguationData":[OD(0.0)],"derivedFrom":[makeQuery(id+"F5.opExtrude","SWEPT_FACE",FACE,{"disambiguationData":[OSD([sQuery(id+"F4.wireOp",EDGE,"E30")])]}),makeQuery(id+"F8.opExtrude","SWEPT_FACE",FACE,{"disambiguationData":[OSD([sQuery(id+"F7.wireOp",EDGE,"E67")])]})]});
            fillet(context, id + "F14", {"entities" : qUnion([Q0, Q1, Q2, Q3, Q4, Q5]), "radius" : 3 * mm, "tangentPropagation" : true, "allowEdgeOverflow" : false});
        }
        {
            var Q0;
            Q0=makeQuery(id+"F1.opExtrude","CAP_EDGE",EDGE,{"disambiguationData":[OSD([sQuery(id+"F0.wireOp",EDGE,"E1.bottom")])],"isStart":false});
            fillet(context, id + "F15", {"entities" : qUnion([Q0]), "radius" : 2 * mm, "tangentPropagation" : true, "allowEdgeOverflow" : false});
        }
        {
            var Q0;
            {var subQ0=sQuery(id+"F0.wireOp",EDGE,"E21.filletArc");var subQ1=sQuery(id+"F0.wireOp",EDGE,"E7");var subQ2=sQuery(id+"F0.wireOp",EDGE,"E6");var subQ3=sQuery(id+"F0.wireOp",EDGE,"E5");var subQ4=sQuery(id+"F0.wireOp",EDGE,"E4");var subQ5=sQuery(id+"F0.wireOp",EDGE,"E22.filletArc");var subQ6=sQuery(id+"F0.wireOp",EDGE,"E1.bottom");var subQ7=sQuery(id+"F0.wireOp",EDGE,"E1.right");var subQ8=sQuery(id+"F0.wireOp",EDGE,"E1.top");var subQ9=sQuery(id+"F0.wireOp",EDGE,"E1.left");var subQ10=sQuery(id+"F0.wireOp",EDGE,"E23.filletArc");var subQ11=sQuery(id+"F0.wireOp",EDGE,"E24.filletArc");Q0=makeQuery(id+"F2.boolean.opBoolean","SPLIT",FACE,{"disambiguationData":[TD([makeQuery(id+"F1.opExtrude","SWEPT_FACE",FACE,{"disambiguationData":[OSD([subQ6])]})])],"derivedFrom":makeQuery(id+"F1.opExtrude","CAP_FACE",FACE,{"disambiguationData":[OSD([subQ6,subQ8,subQ9,subQ7,subQ4,subQ3,subQ2,subQ1,subQ0,subQ5,subQ10,subQ11])],"isStart":true})});}
            var sketch = newSketch(context, id + "F16", { "sketchPlane" : qUnion([Q0])});
            skLineSegment(sketch, "E79", {"start": v(0, 90) * mm, "end": v(0, 120) * mm, "construction": true});
            skCircle(sketch, "E80", {"center": v(0, 120) * mm, "radius": 6 * mm});
            skArc(sketch, "E81", {"start": v(15.14, 120) * mm, "mid": v(0.14, 135.2) * mm, "end": v(-14.86, 120) * mm});
            skLineSegment(sketch, "E82", {"start": v(-14.86, 120) * mm, "end": v(-14.7, 108) * mm});
            skLineSegment(sketch, "E83", {"start": v(15.14, 120) * mm, "end": v(15.14, 108) * mm});
            skLineSegment(sketch, "E84", {"start": v(15.14, 108) * mm, "end": v(33.14, 90) * mm});
            skLineSegment(sketch, "E85", {"start": v(-14.7, 108) * mm, "end": v(-32.7, 90) * mm});
            skLineSegment(sketch, "E86", {"start": v(-122.51, 0) * mm, "end": v(159.5, 0) * mm, "construction": true});
            skPoint(sketch, "E86.startSnap0", {"position": v(-80, 0) * mm});
            skPoint(sketch, "E86.endSnap0", {"position": v(80, 0) * mm});
            skLineSegment(sketch, "E87.MirrorCS", {"start": v(15.14, -120) * mm, "end": v(15.14, -108) * mm});
            skLineSegment(sketch, "E88.MirrorCS", {"start": v(-14.86, -120) * mm, "end": v(-14.7, -108) * mm});
            skLineSegment(sketch, "E89.MirrorCS", {"start": v(-14.7, -108) * mm, "end": v(-32.7, -90) * mm});
            skLineSegment(sketch, "E90.MirrorCS", {"start": v(0, -90) * mm, "end": v(0, -120) * mm, "construction": true});
            skCircle(sketch, "E91.MirrorC", {"center": v(0, -120) * mm, "radius": 6 * mm});
            skLineSegment(sketch, "E92.MirrorCS", {"start": v(15.14, -108) * mm, "end": v(33.14, -90) * mm});
            skArc(sketch, "E93.MirrorCS", {"start": v(15.14, -120) * mm, "mid": v(0.14, -135.2) * mm, "end": v(-14.86, -120) * mm});
            skSolve(sketch);
        }
        {
            var Q0;
            Q0=makeQuery(id+"F16.imprint","IMPRINT",FACE,{"disambiguationData":[TD([[makeQuery(id+"F16.imprint","IMPRINT",EDGE,{"derivedFrom":sQuery(id+"F16.wireOp",EDGE,"E80")}),-1.0]])]});
            var Q1;
            Q1=makeQuery(id+"F16.imprint","IMPRINT",FACE,{"disambiguationData":[TD([[makeQuery(id+"F16.imprint","IMPRINT",EDGE,{"derivedFrom":makeQuery(id+"F1.opExtrude","CAP_EDGE",EDGE,{"disambiguationData":[OSD([sQuery(id+"F0.wireOp",EDGE,"E1.left")])],"isStart":true})}),-1.0]])]});
            var Q2;
            Q2=makeQuery(id+"F16.imprint","IMPRINT",FACE,{"disambiguationData":[TD([[makeQuery(id+"F16.imprint","IMPRINT",EDGE,{"derivedFrom":sQuery(id+"F16.wireOp",EDGE,"E87.MirrorCS")}),1.0]])]});
            var Q3;
            Q3=makeQuery(id+"F2.opExtrude","CAP_FACE",FACE,{"disambiguationData":[OSD([sQuery(id+"F0.wireOp",EDGE,"E12"),sQuery(id+"F0.wireOp",EDGE,"E13"),sQuery(id+"F0.wireOp",EDGE,"E14"),sQuery(id+"F0.wireOp",EDGE,"E15"),sQuery(id+"F0.wireOp",EDGE,"E17.filletArc"),sQuery(id+"F0.wireOp",EDGE,"E18.filletArc"),sQuery(id+"F0.wireOp",EDGE,"E19.filletArc"),sQuery(id+"F0.wireOp",EDGE,"E20.filletArc"),sQuery(id+"F0.wireOp",EDGE,"E25.0"),sQuery(id+"F0.wireOp",EDGE,"E25.1"),sQuery(id+"F0.wireOp",EDGE,"E25.2"),sQuery(id+"F0.wireOp",EDGE,"E25.3"),sQuery(id+"F0.wireOp",EDGE,"E25.4"),sQuery(id+"F0.wireOp",EDGE,"E25.5"),sQuery(id+"F0.wireOp",EDGE,"E25.6"),sQuery(id+"F0.wireOp",EDGE,"E25.7")])],"isStart":false});
            extrude(context, id + "F17", {"entities" : qUnion([Q0, Q1, Q2]), "endBound" : BoundingType.UP_TO_SURFACE, "endBoundEntityFace" : qUnion([Q3]), "depth" : 25 * mm});
        }
    });
